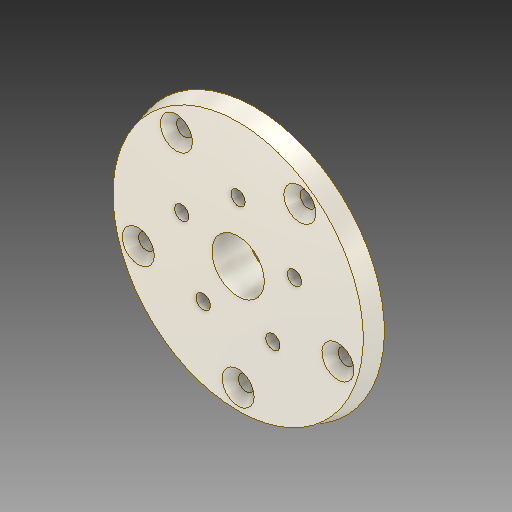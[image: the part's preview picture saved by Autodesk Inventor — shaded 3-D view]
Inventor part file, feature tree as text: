
AUTODESK INVENTOR PART (.ipt)
format: ipt  version: 2019 (Build 230136000, 136)  size: 182,784 bytes
history: native  units: mm
features: sketch x5, extrude x2, hole x2, pattern_circular x1, revolve x1, projected_geometry x1
ambient origin geometry x8: Origin, YZ Plane, XZ Plane, XY Plane, X Axis, Y Axis, Z Axis, Center Point
bodies: Solid1 (feature_tree)
feature tree (12):
  extrude  "Extrusion1"  Depth=108.599mm
  extrude  "Extrusion2"  Depth=7.0mm
  hole  "Hole1"  [1 undecoded]
  hole  "Hole2"  [1 undecoded]
  pattern_circular  "Circular Pattern1"  Count=5 Angle=360.0deg
  revolve  "Revolution1"  Angle=15.0deg
  sketch  "Sketch1"  dims[d0=22.0mm d1=108.599mm]
  sketch  "Sketch2"  dims[d2=7.0mm d3=0.0mm d4=68.0mm]
  sketch  "Sketch3"  dims[d5=8.0mm d6=0.0mm d7=24.84mm]
  sketch  "Sketch4"  dims[d8=6.0mm d9=6.0mm d10=4.0mm d11=2.0mm d12=90.0deg d13=8.0mm d14=20.594885mm d15=44.0mm]
  sketch  "Sketch5"  dims[d16=6.6mm d17=6.0mm d18=13.44mm d19=2.0mm d20=90.0deg d21=8.0mm d22=20.594885mm d23=50.0mm d24=360.0deg d26=15.0deg d27=90.0deg]
  projected_geometry  "Project Cut Edges1"
note: 2 required parameter values undecoded (feature->parameter linkage not recoverable at this tier; creation-order binding heuristic only, values carry confidence <= 0.55)
